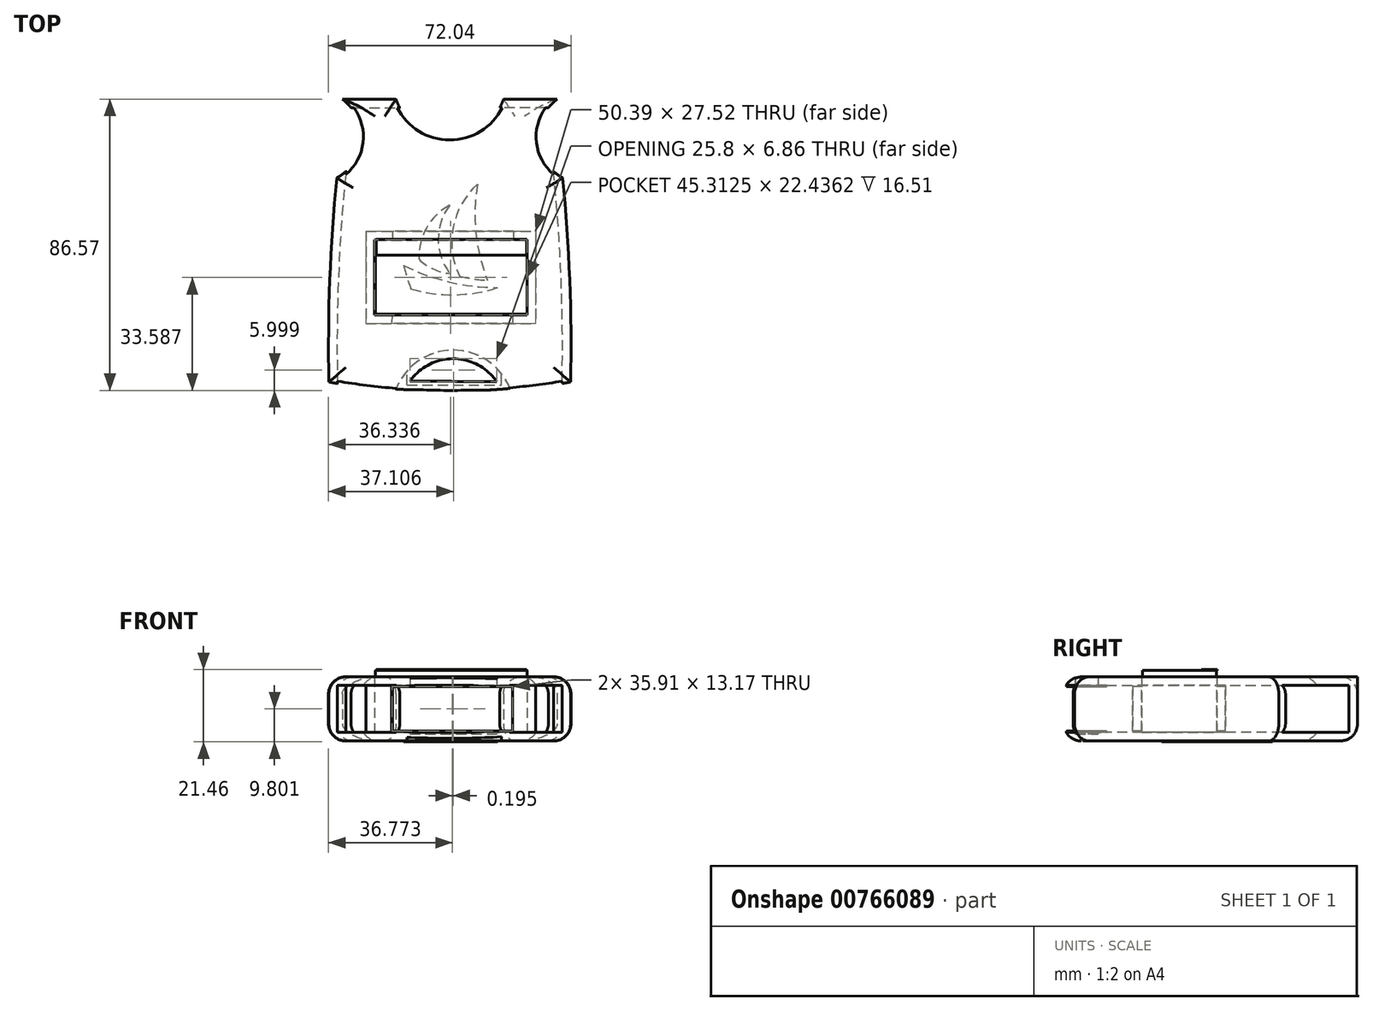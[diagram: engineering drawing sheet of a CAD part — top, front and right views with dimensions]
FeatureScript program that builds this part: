
annotation { "Feature Type Name" : "Feature", "Feature Type Description" : "" }
export const myFeature = defineFeature(function(context is Context, id is Id, definition is map)
    precondition{}
    {
        {
            var Q0;
            Q0=qCreatedBy(makeId("Top.planeOp"),FACE);
            var sketch = newSketch(context, id + "F0", { "sketchPlane" : qUnion([Q0])});
            skArc(sketch, "E0", {"start": v(-33.57, -10.2) * mm, "mid": v(-35.64, -40.5) * mm, "end": v(-35.91, -70.89) * mm});
            skArc(sketch, "E1.MirrorCS", {"start": v(33.57, -10.2) * mm, "mid": v(26.38, 1.05) * mm, "end": v(31.92, 13.2) * mm});
            skArc(sketch, "E2.MirrorCS", {"start": v(33.57, -10.2) * mm, "mid": v(35.64, -40.5) * mm, "end": v(35.91, -70.89) * mm});
            skPoint(sketch, "E3.orphan", {"position": v(13.64, 43.3) * mm});
            skPoint(sketch, "E4.orphan", {"position": v(0, 33.61) * mm});
            skArc(sketch, "E5", {"start": v(-35.91, -70.89) * mm, "mid": v(0, -74.06) * mm, "end": v(35.91, -70.89) * mm});
            skPoint(sketch, "E6.start.orphan", {"position": v(0, 51.54) * mm});
            skArc(sketch, "E7", {"start": v(13.98, -70.81) * mm, "mid": v(1.14, -63.95) * mm, "end": v(-11.81, -70.59) * mm});
            skLineSegment(sketch, "E8", {"start": v(-11.81, -70.59) * mm, "end": v(13.98, -70.81) * mm});
            skLineSegment(sketch, "E9.bottom", {"start": v(-22.34, -28.58) * mm, "end": v(22.97, -28.58) * mm});
            skLineSegment(sketch, "E9.top", {"start": v(-22.34, -51.01) * mm, "end": v(22.97, -51.01) * mm});
            skLineSegment(sketch, "E9.left", {"start": v(-22.34, -28.58) * mm, "end": v(-22.34, -51.01) * mm});
            skLineSegment(sketch, "E9.right", {"start": v(22.97, -28.58) * mm, "end": v(22.97, -51.01) * mm});
            skLineSegment(sketch, "E10", {"start": v(-22.34, -32.1) * mm, "end": v(22.97, -32.1) * mm});
            skPoint(sketch, "E11", {"position": v(31.92, 13.2) * mm});
            skLineSegment(sketch, "E12", {"start": v(31.92, 13.2) * mm, "end": v(15.96, 13.2) * mm});
            skPoint(sketch, "E13.end.orphan", {"position": v(-38.62, 23.94) * mm});
            skLineSegment(sketch, "E14", {"start": v(0, -74.06) * mm, "end": v(0, 38.07) * mm, "construction": true});
            skPoint(sketch, "E15.end.orphan", {"position": v(-16.79, 33.61) * mm});
            skPoint(sketch, "E16.end.orphan", {"position": v(-33.57, 33.61) * mm});
            skPoint(sketch, "E17.MirrorCS.end.orphan", {"position": v(16.79, 33.61) * mm});
            skPoint(sketch, "E17.MirrorCS.start.orphan", {"position": v(19.93, 23.94) * mm});
            skArc(sketch, "E18.MirrorCS", {"start": v(-33.57, -10.2) * mm, "mid": v(-26.38, 1.05) * mm, "end": v(-31.92, 13.2) * mm});
            skLineSegment(sketch, "E19.MirrorCS", {"start": v(-31.92, 13.2) * mm, "end": v(-15.96, 13.2) * mm});
            skArc(sketch, "E20", {"start": v(-15.96, 13.2) * mm, "mid": v(0, 1.76) * mm, "end": v(15.96, 13.2) * mm});
            skPoint(sketch, "E21.orphan", {"position": v(0, 13.2) * mm});
            skSolve(sketch);
        }
        {
            var Q0;
            Q0=makeQuery(id+"F0.imprint","IMPRINT",FACE,{"disambiguationData":[TD([[makeQuery(id+"F0.imprint","IMPRINT",EDGE,{"derivedFrom":sQuery(id+"F0.wireOp",EDGE,"E0")}),1.0]])]});
            extrude(context, id + "F1", {"entities" : qUnion([Q0]), "depth" : 19.05 * mm, "offsetDistance" : 25.4 * mm});
        }
        {
            var Q0;
            Q0=makeQuery(id+"F1.opExtrude","CAP_FACE",FACE,{"disambiguationData":[OSD([sQuery(id+"F0.wireOp",EDGE,"E0"),sQuery(id+"F0.wireOp",EDGE,"E1.MirrorCS"),sQuery(id+"F0.wireOp",EDGE,"E2.MirrorCS"),sQuery(id+"F0.wireOp",EDGE,"E5"),sQuery(id+"F0.wireOp",EDGE,"E7"),sQuery(id+"F0.wireOp",EDGE,"E8"),sQuery(id+"F0.wireOp",EDGE,"E9.bottom"),sQuery(id+"F0.wireOp",EDGE,"E9.top"),sQuery(id+"F0.wireOp",EDGE,"E9.left"),sQuery(id+"F0.wireOp",EDGE,"E9.right"),sQuery(id+"F0.wireOp",EDGE,"E12"),sQuery(id+"F0.wireOp",EDGE,"E18.MirrorCS"),sQuery(id+"F0.wireOp",EDGE,"E19.MirrorCS"),sQuery(id+"F0.wireOp",EDGE,"E20")])],"isStart":false});
            cPlane(context, id + "F2", {"entities" : qUnion([Q0]), "cplaneType" : CPlaneType.OFFSET, "offset" : 0 * mm, "width" : 152.4 * mm, "height" : 152.4 * mm});
        }
        {
            var Q0;
            Q0=qCreatedBy(id+"F2.planeOp",FACE);
            var sketch = newSketch(context, id + "F3", { "sketchPlane" : qUnion([Q0])});
            skLineSegment(sketch, "E22.bottom", {"start": v(-22.07, -28.67) * mm, "end": v(23.03, -28.67) * mm});
            skLineSegment(sketch, "E22.top", {"start": v(-22.07, -50.74) * mm, "end": v(23.03, -50.74) * mm});
            skLineSegment(sketch, "E22.left", {"start": v(-22.07, -28.67) * mm, "end": v(-22.07, -50.74) * mm});
            skLineSegment(sketch, "E22.right", {"start": v(23.03, -28.67) * mm, "end": v(23.03, -50.74) * mm});
            skSolve(sketch);
        }
        {
            var Q0;
            Q0=makeQuery(id+"F3.imprint","IMPRINT",FACE,{"disambiguationData":[TD([[makeQuery(id+"F3.imprint","IMPRINT",EDGE,{"derivedFrom":sQuery(id+"F3.wireOp",EDGE,"E22.bottom")}),-1.0]])]});
            extrude(context, id + "F4", {"entities" : qUnion([Q0]), "operationType" : NewBodyOperationType.ADD, "depth" : 1.9 * mm, "offsetDistance" : 25.4 * mm});
        }
        {
            var Q0;
            Q0=makeQuery(id+"F4.opExtrude","CAP_FACE",FACE,{"disambiguationData":[OSD([sQuery(id+"F3.wireOp",EDGE,"E22.bottom"),sQuery(id+"F3.wireOp",EDGE,"E22.top"),sQuery(id+"F3.wireOp",EDGE,"E22.left"),sQuery(id+"F3.wireOp",EDGE,"E22.right")])],"isStart":false});
            cPlane(context, id + "F5", {"entities" : qUnion([Q0]), "cplaneType" : CPlaneType.OFFSET, "offset" : 0 * mm, "width" : 152.4 * mm, "height" : 152.4 * mm});
        }
        {
            var Q0;
            Q0=qCreatedBy(id+"F5.planeOp",FACE);
            var sketch = newSketch(context, id + "F6", { "sketchPlane" : qUnion([Q0])});
            skLineSegment(sketch, "E23.bottom", {"start": v(-21.83, -28.43) * mm, "end": v(22.85, -28.43) * mm});
            skLineSegment(sketch, "E23.top", {"start": v(-21.83, -33.11) * mm, "end": v(22.85, -33.11) * mm});
            skLineSegment(sketch, "E23.left", {"start": v(-21.83, -28.43) * mm, "end": v(-21.83, -33.11) * mm});
            skLineSegment(sketch, "E23.right", {"start": v(22.85, -28.43) * mm, "end": v(22.85, -33.11) * mm});
            skSolve(sketch);
        }
        {
            var Q0;
            Q0=makeQuery(id+"F6.imprint","IMPRINT",FACE,{"disambiguationData":[TD([[makeQuery(id+"F6.imprint","IMPRINT",EDGE,{"derivedFrom":sQuery(id+"F6.wireOp",EDGE,"E23.bottom")}),-1.0]])]});
            extrude(context, id + "F7", {"entities" : qUnion([Q0]), "operationType" : NewBodyOperationType.ADD, "depth" : 0.25 * mm, "offsetDistance" : 25.4 * mm});
        }
        {
            var Q0;
            Q0=makeQuery(id+"F1.opExtrude","SWEPT_FACE",FACE,{"disambiguationData":[OSD([sQuery(id+"F0.wireOp",EDGE,"E1.MirrorCS")])]});
            var Q1;
            Q1=makeQuery(id+"F1.opExtrude","SWEPT_FACE",FACE,{"disambiguationData":[OSD([sQuery(id+"F0.wireOp",EDGE,"E5")])]});
            var Q2;
            Q2=makeQuery(id+"F1.opExtrude","SWEPT_FACE",FACE,{"disambiguationData":[OSD([sQuery(id+"F0.wireOp",EDGE,"E18.MirrorCS")])]});
            var Q3;
            Q3=makeQuery(id+"F1.opExtrude","SWEPT_FACE",FACE,{"disambiguationData":[OSD([sQuery(id+"F0.wireOp",EDGE,"E20")])]});
            shell(context, id + "F8", {"entities" : qUnion([Q0, Q1, Q2, Q3]), "thickness" : 2.54 * mm});
        }
        {
            var Q0;
            Q0=makeQuery(id+"F1.opExtrude","CAP_EDGE",EDGE,{"disambiguationData":[OSD([sQuery(id+"F0.wireOp",EDGE,"E20")])],"isStart":false});
            var Q1;
            Q1=makeQuery(id+"F1.opExtrude","CAP_EDGE",EDGE,{"disambiguationData":[OSD([sQuery(id+"F0.wireOp",EDGE,"E19.MirrorCS")])],"isStart":false});
            var Q2;
            Q2=makeQuery(id+"F1.opExtrude","CAP_EDGE",EDGE,{"disambiguationData":[OSD([sQuery(id+"F0.wireOp",EDGE,"E18.MirrorCS")])],"isStart":false});
            var Q3;
            Q3=makeQuery(id+"F1.opExtrude","CAP_EDGE",EDGE,{"disambiguationData":[OSD([sQuery(id+"F0.wireOp",EDGE,"E0")])],"isStart":false});
            var Q4;
            Q4=makeQuery(id+"F1.opExtrude","CAP_EDGE",EDGE,{"disambiguationData":[OSD([sQuery(id+"F0.wireOp",EDGE,"E5")])],"isStart":false});
            var Q5;
            Q5=makeQuery(id+"F1.opExtrude","CAP_EDGE",EDGE,{"disambiguationData":[OSD([sQuery(id+"F0.wireOp",EDGE,"E2.MirrorCS")])],"isStart":false});
            var Q6;
            Q6=makeQuery(id+"F1.opExtrude","CAP_EDGE",EDGE,{"disambiguationData":[OSD([sQuery(id+"F0.wireOp",EDGE,"E1.MirrorCS")])],"isStart":false});
            var Q7;
            Q7=makeQuery(id+"F1.opExtrude","CAP_EDGE",EDGE,{"disambiguationData":[OSD([sQuery(id+"F0.wireOp",EDGE,"E12")])],"isStart":true});
            var Q8;
            Q8=makeQuery(id+"F1.opExtrude","CAP_EDGE",EDGE,{"disambiguationData":[OSD([sQuery(id+"F0.wireOp",EDGE,"E1.MirrorCS")])],"isStart":true});
            var Q9;
            Q9=makeQuery(id+"F1.opExtrude","CAP_EDGE",EDGE,{"disambiguationData":[OSD([sQuery(id+"F0.wireOp",EDGE,"E2.MirrorCS")])],"isStart":true});
            var Q10;
            Q10=makeQuery(id+"F1.opExtrude","CAP_EDGE",EDGE,{"disambiguationData":[OSD([sQuery(id+"F0.wireOp",EDGE,"E5")])],"isStart":true});
            var Q11;
            Q11=makeQuery(id+"F1.opExtrude","CAP_EDGE",EDGE,{"disambiguationData":[OSD([sQuery(id+"F0.wireOp",EDGE,"E0")])],"isStart":true});
            var Q12;
            Q12=makeQuery(id+"F1.opExtrude","CAP_EDGE",EDGE,{"disambiguationData":[OSD([sQuery(id+"F0.wireOp",EDGE,"E18.MirrorCS")])],"isStart":true});
            var Q13;
            Q13=makeQuery(id+"F1.opExtrude","CAP_EDGE",EDGE,{"disambiguationData":[OSD([sQuery(id+"F0.wireOp",EDGE,"E19.MirrorCS")])],"isStart":true});
            var Q14;
            Q14=makeQuery(id+"F1.opExtrude","CAP_EDGE",EDGE,{"disambiguationData":[OSD([sQuery(id+"F0.wireOp",EDGE,"E20")])],"isStart":true});
            fillet(context, id + "F9", {"entities" : qUnion([Q0, Q1, Q2, Q3, Q4, Q5, Q6, Q7, Q8, Q9, Q10, Q11, Q12, Q13, Q14]), "radius" : 5.08 * mm, "tangentPropagation" : true, "allowEdgeOverflow" : false});
        }
        {
            var Q0;
            Q0=makeQuery(id+"F1.opExtrude","CAP_FACE",FACE,{"disambiguationData":[OSD([sQuery(id+"F0.wireOp",EDGE,"E0"),sQuery(id+"F0.wireOp",EDGE,"E1.MirrorCS"),sQuery(id+"F0.wireOp",EDGE,"E2.MirrorCS"),sQuery(id+"F0.wireOp",EDGE,"E5"),sQuery(id+"F0.wireOp",EDGE,"E7"),sQuery(id+"F0.wireOp",EDGE,"E8"),sQuery(id+"F0.wireOp",EDGE,"E9.bottom"),sQuery(id+"F0.wireOp",EDGE,"E9.top"),sQuery(id+"F0.wireOp",EDGE,"E9.left"),sQuery(id+"F0.wireOp",EDGE,"E9.right"),sQuery(id+"F0.wireOp",EDGE,"E12"),sQuery(id+"F0.wireOp",EDGE,"E18.MirrorCS"),sQuery(id+"F0.wireOp",EDGE,"E19.MirrorCS"),sQuery(id+"F0.wireOp",EDGE,"E20")])],"isStart":true});
            cPlane(context, id + "F10", {"entities" : qUnion([Q0]), "cplaneType" : CPlaneType.OFFSET, "offset" : 0 * mm, "width" : 152.4 * mm, "height" : 152.4 * mm});
        }
        {
            var Q0;
            Q0=qCreatedBy(id+"F10.planeOp",FACE);
            var sketch = newSketch(context, id + "F11", { "sketchPlane" : qUnion([Q0])});
            skLineSegment(sketch, "E24.bottom", {"start": v(-25.1, 55.1) * mm, "end": v(26.13, 55.1) * mm});
            skLineSegment(sketch, "E24.top", {"start": v(-25.1, 22.58) * mm, "end": v(26.13, 22.58) * mm});
            skLineSegment(sketch, "E24.left", {"start": v(-25.1, 55.1) * mm, "end": v(-25.1, 22.58) * mm});
            skLineSegment(sketch, "E24.right", {"start": v(26.13, 55.1) * mm, "end": v(26.13, 22.58) * mm});
            skSolve(sketch);
        }
        {
            var Q0;
            Q0=makeQuery(id+"F11.imprint","IMPRINT",FACE,{"disambiguationData":[TD([[makeQuery(id+"F11.imprint","IMPRINT",EDGE,{"derivedFrom":sQuery(id+"F11.wireOp",EDGE,"E24.bottom")}),-1.0]])]});
            extrude(context, id + "F12", {"entities" : qUnion([Q0]), "operationType" : NewBodyOperationType.ADD, "oppositeDirection" : true, "depth" : 2.54 * mm, "offsetDistance" : 25.4 * mm});
        }
        {
            var Q0;
            Q0=makeQuery(id+"F8.opShell","OFFSET_FACE",FACE,{"disambiguationData":[OSD([sQuery(id+"F0.wireOp",EDGE,"E8")])]});
            cPlane(context, id + "F13", {"entities" : qUnion([Q0]), "cplaneType" : CPlaneType.OFFSET, "offset" : 0 * mm, "width" : 152.4 * mm, "height" : 152.4 * mm});
        }
        {
            var Q0;
            Q0=qCreatedBy(id+"F13.planeOp",FACE);
            var sketch = newSketch(context, id + "F14", { "sketchPlane" : qUnion([Q0])});
            skLineSegment(sketch, "E25.bottom", {"start": v(-16.76, 16.13) * mm, "end": v(19.15, 16.13) * mm});
            skLineSegment(sketch, "E25.top", {"start": v(-16.76, 2.97) * mm, "end": v(19.15, 2.97) * mm});
            skLineSegment(sketch, "E25.left", {"start": v(-16.76, 16.13) * mm, "end": v(-16.76, 2.97) * mm});
            skLineSegment(sketch, "E25.right", {"start": v(19.15, 16.13) * mm, "end": v(19.15, 2.97) * mm});
            skSolve(sketch);
        }
        {
            var Q0;
            Q0=makeQuery(id+"F14.imprint","IMPRINT",FACE,{"disambiguationData":[TD([[makeQuery(id+"F14.imprint","IMPRINT",EDGE,{"derivedFrom":sQuery(id+"F14.wireOp",EDGE,"E25.bottom")}),-1.0]])]});
            extrude(context, id + "F15", {"entities" : qUnion([Q0]), "operationType" : NewBodyOperationType.REMOVE, "oppositeDirection" : true, "depth" : 76.2 * mm, "offsetDistance" : 25.4 * mm});
        }
        {
            var Q0;
            Q0=makeQuery(id+"F12.boolean.opBoolean","MERGE",FACE,{"derivedFrom":[makeQuery(id+"F1.opExtrude","CAP_FACE",FACE,{"disambiguationData":[OSD([sQuery(id+"F0.wireOp",EDGE,"E0"),sQuery(id+"F0.wireOp",EDGE,"E1.MirrorCS"),sQuery(id+"F0.wireOp",EDGE,"E2.MirrorCS"),sQuery(id+"F0.wireOp",EDGE,"E5"),sQuery(id+"F0.wireOp",EDGE,"E7"),sQuery(id+"F0.wireOp",EDGE,"E8"),sQuery(id+"F0.wireOp",EDGE,"E9.bottom"),sQuery(id+"F0.wireOp",EDGE,"E9.top"),sQuery(id+"F0.wireOp",EDGE,"E9.left"),sQuery(id+"F0.wireOp",EDGE,"E9.right"),sQuery(id+"F0.wireOp",EDGE,"E12"),sQuery(id+"F0.wireOp",EDGE,"E18.MirrorCS"),sQuery(id+"F0.wireOp",EDGE,"E19.MirrorCS"),sQuery(id+"F0.wireOp",EDGE,"E20")])],"isStart":true}),makeQuery(id+"F12.opExtrude","CAP_FACE",FACE,{"disambiguationData":[OSD([sQuery(id+"F11.wireOp",EDGE,"E24.bottom"),sQuery(id+"F11.wireOp",EDGE,"E24.top"),sQuery(id+"F11.wireOp",EDGE,"E24.left"),sQuery(id+"F11.wireOp",EDGE,"E24.right")])],"isStart":true})]});
            cPlane(context, id + "F16", {"entities" : qUnion([Q0]), "cplaneType" : CPlaneType.OFFSET, "offset" : 0 * mm, "width" : 152.4 * mm, "height" : 152.4 * mm});
        }
        {
            var Q0;
            Q0=qCreatedBy(id+"F16.planeOp",FACE);
            var sketch = newSketch(context, id + "F17", { "sketchPlane" : qUnion([Q0])});
            skLineSegment(sketch, "E26.bottom", {"start": v(-12.7, 71.72) * mm, "end": v(15.37, 71.72) * mm});
            skLineSegment(sketch, "E26.top", {"start": v(-12.7, 60.95) * mm, "end": v(15.37, 60.95) * mm});
            skLineSegment(sketch, "E26.left", {"start": v(-12.7, 71.72) * mm, "end": v(-12.7, 60.95) * mm});
            skLineSegment(sketch, "E26.right", {"start": v(15.37, 71.72) * mm, "end": v(15.37, 60.95) * mm});
            skSolve(sketch);
        }
        {
            var Q0;
            Q0=makeQuery(id+"F17.imprint","IMPRINT",FACE,{"disambiguationData":[TD([[makeQuery(id+"F17.imprint","IMPRINT",EDGE,{"derivedFrom":sQuery(id+"F17.wireOp",EDGE,"E26.bottom")}),-1.0]])]});
            extrude(context, id + "F18", {"entities" : qUnion([Q0]), "operationType" : NewBodyOperationType.ADD, "oppositeDirection" : true, "depth" : 2.03 * mm, "offsetDistance" : 25.4 * mm});
        }
        {
            var Q0;
            Q0=makeQuery(id+"F18.opExtrude","CAP_EDGE",EDGE,{"disambiguationData":[OSD([sQuery(id+"F17.wireOp",EDGE,"E26.bottom")])],"isStart":true});
            fillet(context, id + "F19", {"entities" : qUnion([Q0]), "radius" : 5.08 * mm, "tangentPropagation" : true, "allowEdgeOverflow" : false});
        }
        {
            var Q0;
            Q0=qCreatedBy(makeId("Top.planeOp"),FACE);
            var sketch = newSketch(context, id + "F20", { "sketchPlane" : qUnion([Q0])});
            skArc(sketch, "E27", {"start": v(-13.7, -36.26) * mm, "mid": v(-0.11, -41.14) * mm, "end": v(14.22, -42.82) * mm});
            skArc(sketch, "E28", {"start": v(-13.7, -36.26) * mm, "mid": v(-12.71, -39.77) * mm, "end": v(-11.53, -43.22) * mm});
            skArc(sketch, "E29", {"start": v(-11.53, -43.22) * mm, "mid": v(1.38, -44.95) * mm, "end": v(14.22, -42.82) * mm});
            skArc(sketch, "E30", {"start": v(2.87, -39.4) * mm, "mid": v(7.01, -40.23) * mm, "end": v(11.22, -40.65) * mm});
            skPoint(sketch, "E31", {"position": v(-9.18, -34.36) * mm});
            skPoint(sketch, "E32", {"position": v(0, -18.27) * mm});
            skPoint(sketch, "E32.positionSnap0", {"position": v(0, -38.57) * mm});
            skPoint(sketch, "E33", {"position": v(8.22, -12.04) * mm});
            skPoint(sketch, "E34", {"position": v(0, -34.65) * mm});
            skPoint(sketch, "E35", {"position": v(2.87, -39.4) * mm});
            skArc(sketch, "E36", {"start": v(8.22, -12.04) * mm, "mid": v(7.78, -26.55) * mm, "end": v(11.22, -40.65) * mm});
            skArc(sketch, "E37", {"start": v(8.22, -12.04) * mm, "mid": v(1.02, -24.83) * mm, "end": v(2.87, -39.4) * mm});
            skArc(sketch, "E38", {"start": v(0, -18.27) * mm, "mid": v(-3.42, -28.42) * mm, "end": v(0, -38.57) * mm});
            skArc(sketch, "E39", {"start": v(0, -18.27) * mm, "mid": v(-6.87, -25) * mm, "end": v(-9.18, -34.36) * mm});
            skArc(sketch, "E40", {"start": v(-9.18, -34.36) * mm, "mid": v(-4.96, -37.27) * mm, "end": v(0, -38.57) * mm});
            skSolve(sketch);
        }
        {
            var Q0;
            Q0=makeQuery(id+"F20.imprint","IMPRINT",FACE,{"disambiguationData":[TD([[makeQuery(id+"F20.imprint","IMPRINT",EDGE,{"derivedFrom":sQuery(id+"F20.wireOp",EDGE,"E30")}),1.0]])]});
            var Q1;
            Q1=makeQuery(id+"F20.imprint","IMPRINT",FACE,{"disambiguationData":[TD([[makeQuery(id+"F20.imprint","IMPRINT",EDGE,{"derivedFrom":sQuery(id+"F20.wireOp",EDGE,"E38")}),-1.0]])]});
            var Q2;
            Q2=makeQuery(id+"F20.imprint","IMPRINT",FACE,{"disambiguationData":[TD([[makeQuery(id+"F20.imprint","IMPRINT",EDGE,{"derivedFrom":sQuery(id+"F20.wireOp",EDGE,"E27")}),-1.0]])]});
            extrude(context, id + "F21", {"entities" : qUnion([Q0, Q1, Q2]), "operationType" : NewBodyOperationType.ADD, "oppositeDirection" : true, "depth" : 0.25 * mm, "offsetDistance" : 25.4 * mm});
        }
    });
